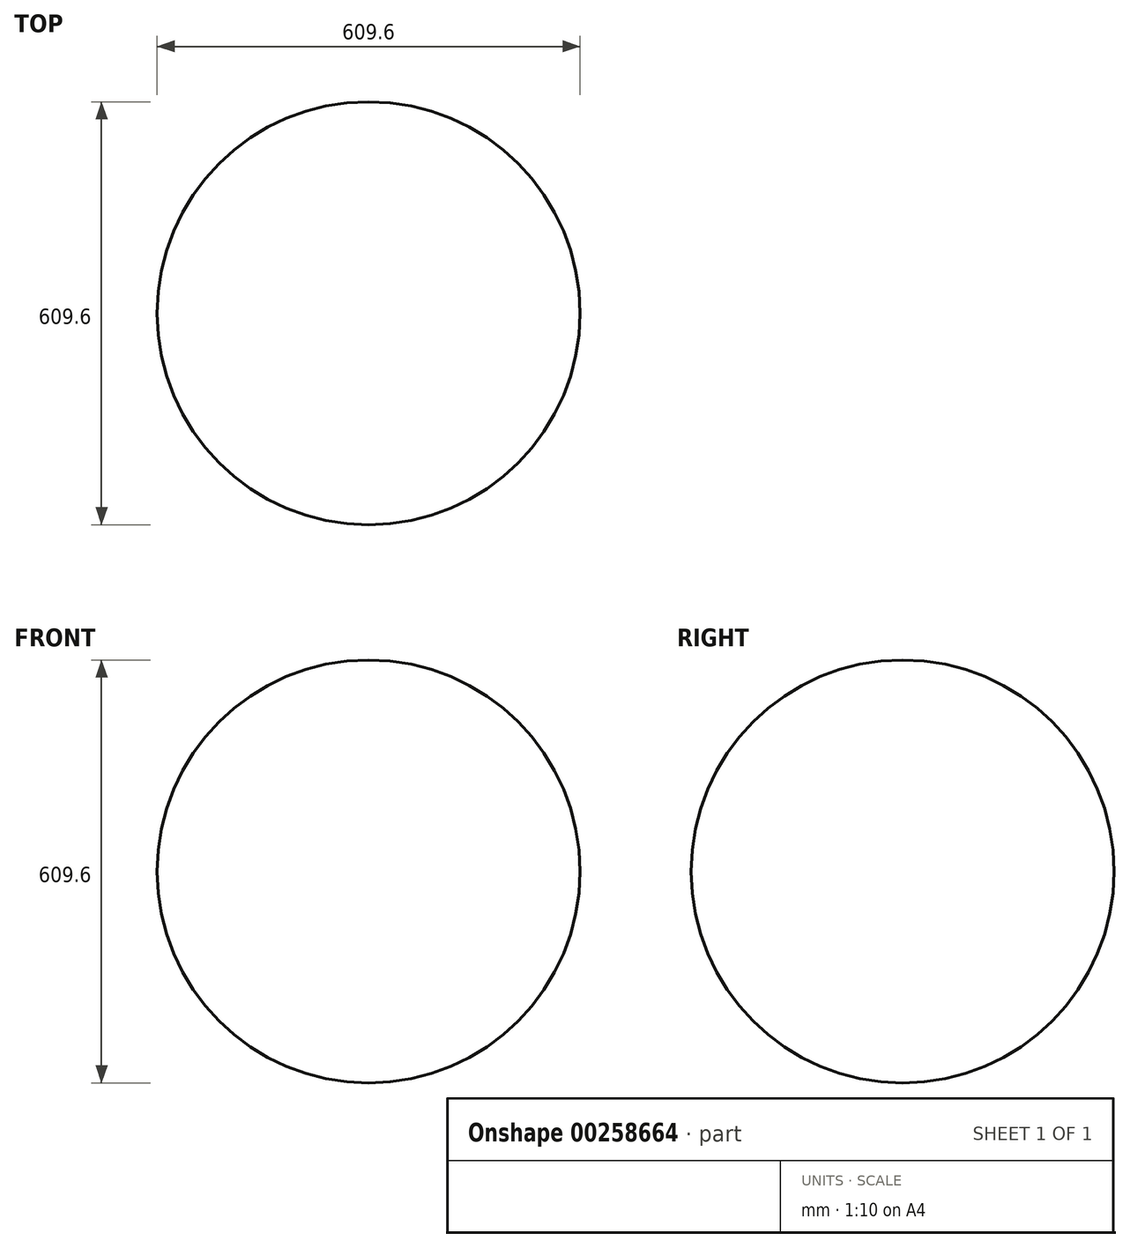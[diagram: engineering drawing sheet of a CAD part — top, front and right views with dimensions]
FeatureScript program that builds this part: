
annotation { "Feature Type Name" : "Feature", "Feature Type Description" : "" }
export const myFeature = defineFeature(function(context is Context, id is Id, definition is map)
    precondition{}
    {
        {
            var Q0;
            Q0=qCreatedBy(makeId("Front.planeOp"),FACE);
            var sketch = newSketch(context, id + "F0", { "sketchPlane" : qUnion([Q0])});
            skArc(sketch, "E0", {"start": v(0, -304.8) * mm, "mid": v(304.8, 0) * mm, "end": v(0, 304.8) * mm});
            skLineSegment(sketch, "E1", {"start": v(0, 304.8) * mm, "end": v(0, -304.8) * mm});
            skSolve(sketch);
        }
        {
            var Q0;
            Q0 = qSketchRegion(id + "F0", true);
            var Q1;
            Q1=sQuery(id+"F0.wireOp",EDGE,"E1");
            revolve(context, id + "F1", {"entities" : qUnion([Q0]), "axis" : qUnion([Q1]), "revolveType" : RevolveType.FULL});
        }
    });
